# Revit family: Балансировочный клапан с диафрагмой для систем питьевого водоснабжения 4017 MW (LF-MF)
name_source: partatom
category: Rohrzubehör
units: mm (PartAtom-declared; Revit-internal decimal feet)

## family parameters
Arbeitsebenenbasiert = Nein
Beim Laden mit Abzugskörper schneiden = Nein
Bemaßung runder Anschluss = Durchmesser verwenden
Gemeinsam genutzt = Nein
Immer vertikal = Ja
OmniClass-Nummer = 23.65.55.14
OmniClass-Titel = Valves for Liquid Services
Teiletyp = Unterbricht

## types (2) — shared parameters
H02 = 13 mm
Hersteller = HERZ Armaturen Ges.m.b.H.
O-Ring = EPDM
R01 = 12 mm  [stored 0.0393701 ft]
R02 = 9.5 mm  [stored 0.031168 ft]
R03 = 21.5 mm  [stored 0.0705381 ft]
S03 = 60 mm  [stored 0.19685 ft]
SCRNCODE = 04;00;02
SCRNSEQ = FW;SBT_TYP_FW="109";2
SW01 = 60.00°
URL = www.herz-armaturen.ru
W01 = 45.00°
Исполнение = В соответствии с нормами BS 7350 PN20, серия В, балансировочный клапан с наклонным шпинделем производится из медных сплавов.
Все металлические части, контактирующие с водой, изготовлены из латуни, устойчивой к селективной цинковой коррозии.
Кран-букса - с неподнимающимся шпинделем.
Корпус = латунь, устойчивая к селективной цинковой коррозии
Макс. перепад давления на закрытом седле = 1000000.0 Pa
Макс. рабочая температура при 10 бар = 85 °C
Макс. рабочее давление при 20 °C = 2000000.0 Pa
Маховик = пластик, цвет - зеленый
Область применения = Для перекрытия трубопроводов и регулирования систем питьевого водоснабжения в зданиях или для гидравлической балансировки водоподающих трубопроводов.
Примечание = В соответствии со статьей 33 Регламента REACH (Registration; Evaluation; Authorisation; Restriction of Chemicals) (EC № 1907/2006) мы обязаны указать, что свинец внесен в список SVHC (Substances of Very High Concern - вещества очень высокой важности) и весовой процент свинца во всех латунных компонентах заводского изготовления в наших изделиях, превышает 0,1 % (w/w) (CAS: 7439-92-1 / EINECS: 231-100-4).
Поскольку свинец является легирующим компонентом сплава, прямое негативное влияние исключается, и поэтому дополнительной информации о безопасном использовании не требуется.
Среда = Питьевая вода
zero-valued in all types: E00, Vorgabe-Ansicht

## per-type parameters (varying)
| type | LF | MF |
| LF | Ja | Nein |
| MF | Nein | Ja |

note: [stored X ft] marks values corroborated as IEEE doubles in the binary element streams (Revit-internal decimal feet)
